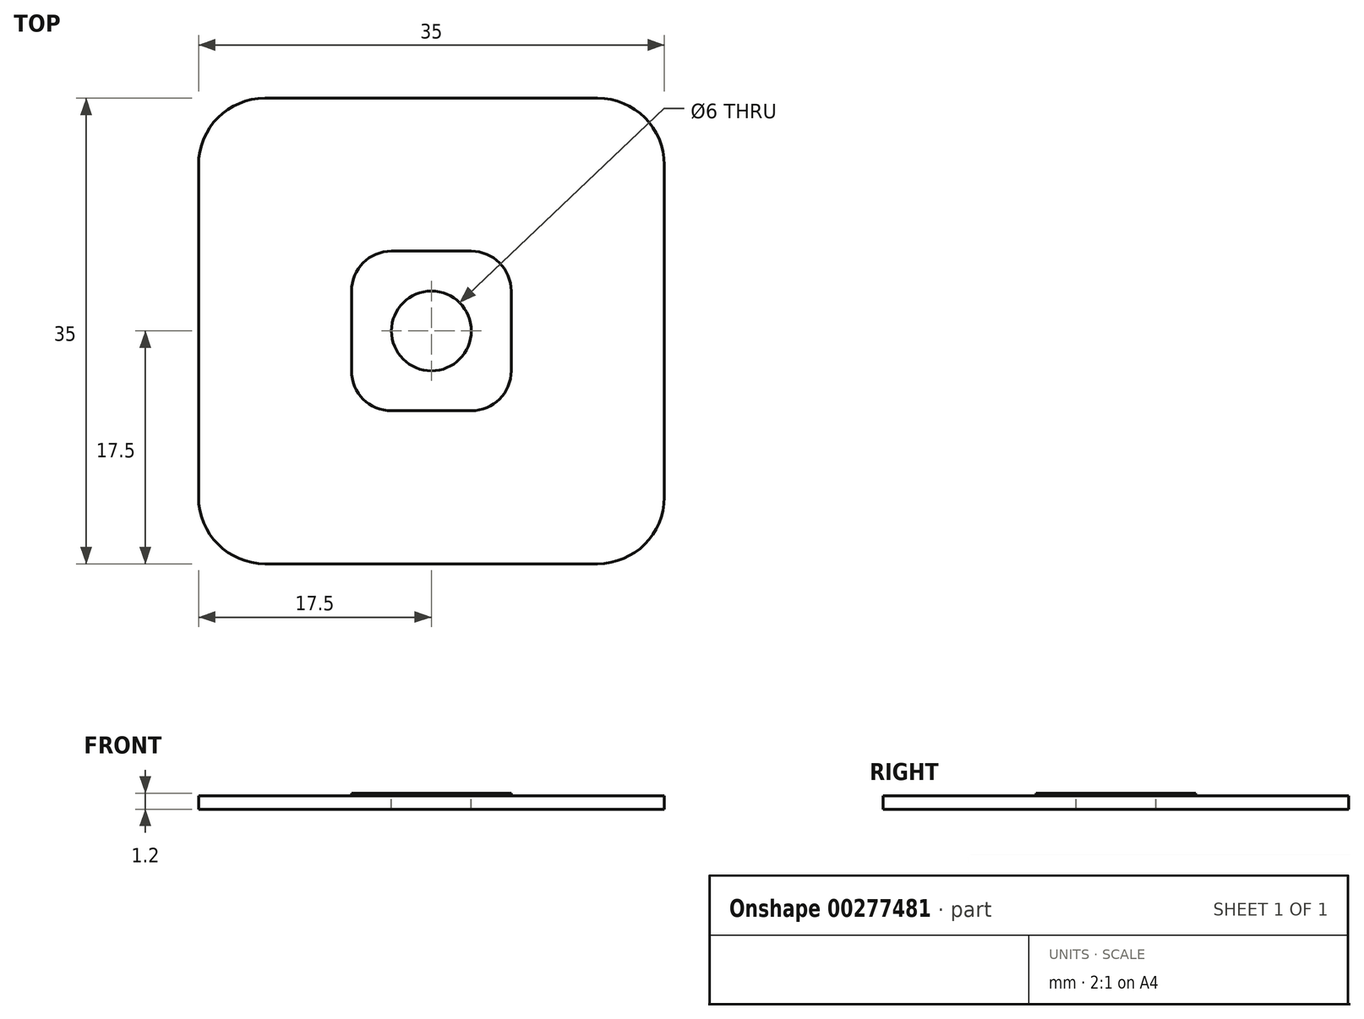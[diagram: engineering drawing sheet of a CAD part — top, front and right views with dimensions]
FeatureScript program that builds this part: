
annotation { "Feature Type Name" : "Feature", "Feature Type Description" : "" }
export const myFeature = defineFeature(function(context is Context, id is Id, definition is map)
    precondition{}
    {
        {
            var Q0;
            Q0=qCreatedBy(makeId("Top.planeOp"),FACE);
            var sketch = newSketch(context, id + "F0", { "sketchPlane" : qUnion([Q0])});
            skLineSegment(sketch, "E0.bottom", {"start": v(17.5, 17.5) * mm, "end": v(-17.5, 17.5) * mm});
            skLineSegment(sketch, "E0.top", {"start": v(17.5, -17.5) * mm, "end": v(-17.5, -17.5) * mm});
            skLineSegment(sketch, "E0.left", {"start": v(17.5, 17.5) * mm, "end": v(17.5, -17.5) * mm});
            skLineSegment(sketch, "E0.right", {"start": v(-17.5, 17.5) * mm, "end": v(-17.5, -17.5) * mm});
            skPoint(sketch, "E0.middle", {"position": v(0, 0) * mm});
            skLineSegment(sketch, "E1.bottom", {"start": v(6, 6) * mm, "end": v(-6, 6) * mm});
            skLineSegment(sketch, "E1.top", {"start": v(6, -6) * mm, "end": v(-6, -6) * mm});
            skLineSegment(sketch, "E1.left", {"start": v(6, 6) * mm, "end": v(6, -6) * mm});
            skLineSegment(sketch, "E1.right", {"start": v(-6, 6) * mm, "end": v(-6, -6) * mm});
            skSolve(sketch);
        }
        {
            var Q0;
            Q0=makeQuery(id+"F0.imprint","IMPRINT",FACE,{"disambiguationData":[TD([[makeQuery(id+"F0.imprint","IMPRINT",EDGE,{"derivedFrom":sQuery(id+"F0.wireOp",EDGE,"E0.bottom")}),1.0]])]});
            extrude(context, id + "F1", {"entities" : qUnion([Q0]), "depth" : 1 * mm});
        }
        {
            var Q0;
            Q0=makeQuery(id+"F0.imprint","IMPRINT",FACE,{"disambiguationData":[TD([[makeQuery(id+"F0.imprint","IMPRINT",EDGE,{"derivedFrom":sQuery(id+"F0.wireOp",EDGE,"E1.bottom")}),1.0]])]});
            extrude(context, id + "F2", {"entities" : qUnion([Q0]), "operationType" : NewBodyOperationType.ADD, "depth" : 1.2 * mm});
        }
        {
            var Q0;
            Q0=makeQuery(id+"F2.opExtrude","SWEPT_EDGE",EDGE,{"disambiguationData":[OSD([sQuery(id+"F0.wireOp",EDGE,"E1.top"),sQuery(id+"F0.wireOp",EDGE,"E1.right")])]});
            var Q1;
            Q1=makeQuery(id+"F2.opExtrude","SWEPT_EDGE",EDGE,{"disambiguationData":[OSD([sQuery(id+"F0.wireOp",EDGE,"E1.top"),sQuery(id+"F0.wireOp",EDGE,"E1.left")])]});
            var Q2;
            Q2=makeQuery(id+"F2.opExtrude","SWEPT_EDGE",EDGE,{"disambiguationData":[OSD([sQuery(id+"F0.wireOp",EDGE,"E1.bottom"),sQuery(id+"F0.wireOp",EDGE,"E1.left")])]});
            var Q3;
            Q3=makeQuery(id+"F2.opExtrude","SWEPT_EDGE",EDGE,{"disambiguationData":[OSD([sQuery(id+"F0.wireOp",EDGE,"E1.bottom"),sQuery(id+"F0.wireOp",EDGE,"E1.right")])]});
            fillet(context, id + "F3", {"entities" : qUnion([Q0, Q1, Q2, Q3]), "radius" : 3 * mm, "tangentPropagation" : true, "allowEdgeOverflow" : false});
        }
        {
            var Q0;
            Q0=makeQuery(id+"F1.opExtrude","SWEPT_EDGE",EDGE,{"disambiguationData":[OSD([sQuery(id+"F0.wireOp",EDGE,"E0.top"),sQuery(id+"F0.wireOp",EDGE,"E0.right")])]});
            var Q1;
            Q1=makeQuery(id+"F1.opExtrude","SWEPT_EDGE",EDGE,{"disambiguationData":[OSD([sQuery(id+"F0.wireOp",EDGE,"E0.top"),sQuery(id+"F0.wireOp",EDGE,"E0.left")])]});
            var Q2;
            Q2=makeQuery(id+"F1.opExtrude","SWEPT_EDGE",EDGE,{"disambiguationData":[OSD([sQuery(id+"F0.wireOp",EDGE,"E0.bottom"),sQuery(id+"F0.wireOp",EDGE,"E0.left")])]});
            var Q3;
            Q3=makeQuery(id+"F1.opExtrude","SWEPT_EDGE",EDGE,{"disambiguationData":[OSD([sQuery(id+"F0.wireOp",EDGE,"E0.bottom"),sQuery(id+"F0.wireOp",EDGE,"E0.right")])]});
            fillet(context, id + "F4", {"entities" : qUnion([Q0, Q1, Q2, Q3]), "radius" : 5 * mm, "tangentPropagation" : true, "allowEdgeOverflow" : false});
        }
        {
            var Q0;
            Q0=makeQuery(id+"F2.opExtrude","CAP_FACE",FACE,{"disambiguationData":[OSD([sQuery(id+"F0.wireOp",EDGE,"E1.bottom"),sQuery(id+"F0.wireOp",EDGE,"E1.top"),sQuery(id+"F0.wireOp",EDGE,"E1.left"),sQuery(id+"F0.wireOp",EDGE,"E1.right")])],"isStart":false});
            var sketch = newSketch(context, id + "F5", { "sketchPlane" : qUnion([Q0])});
            skCircle(sketch, "E2", {"center": v(0, 0) * mm, "radius": 3 * mm});
            skSolve(sketch);
        }
        {
            var Q0;
            Q0=makeQuery(id+"F5.imprint","IMPRINT",FACE,{"disambiguationData":[TD([[makeQuery(id+"F5.imprint","IMPRINT",EDGE,{"derivedFrom":sQuery(id+"F5.wireOp",EDGE,"E2")}),1.0]])]});
            extrude(context, id + "F6", {"entities" : qUnion([Q0]), "operationType" : NewBodyOperationType.REMOVE, "oppositeDirection" : true, "depth" : 25 * mm});
        }
    });
